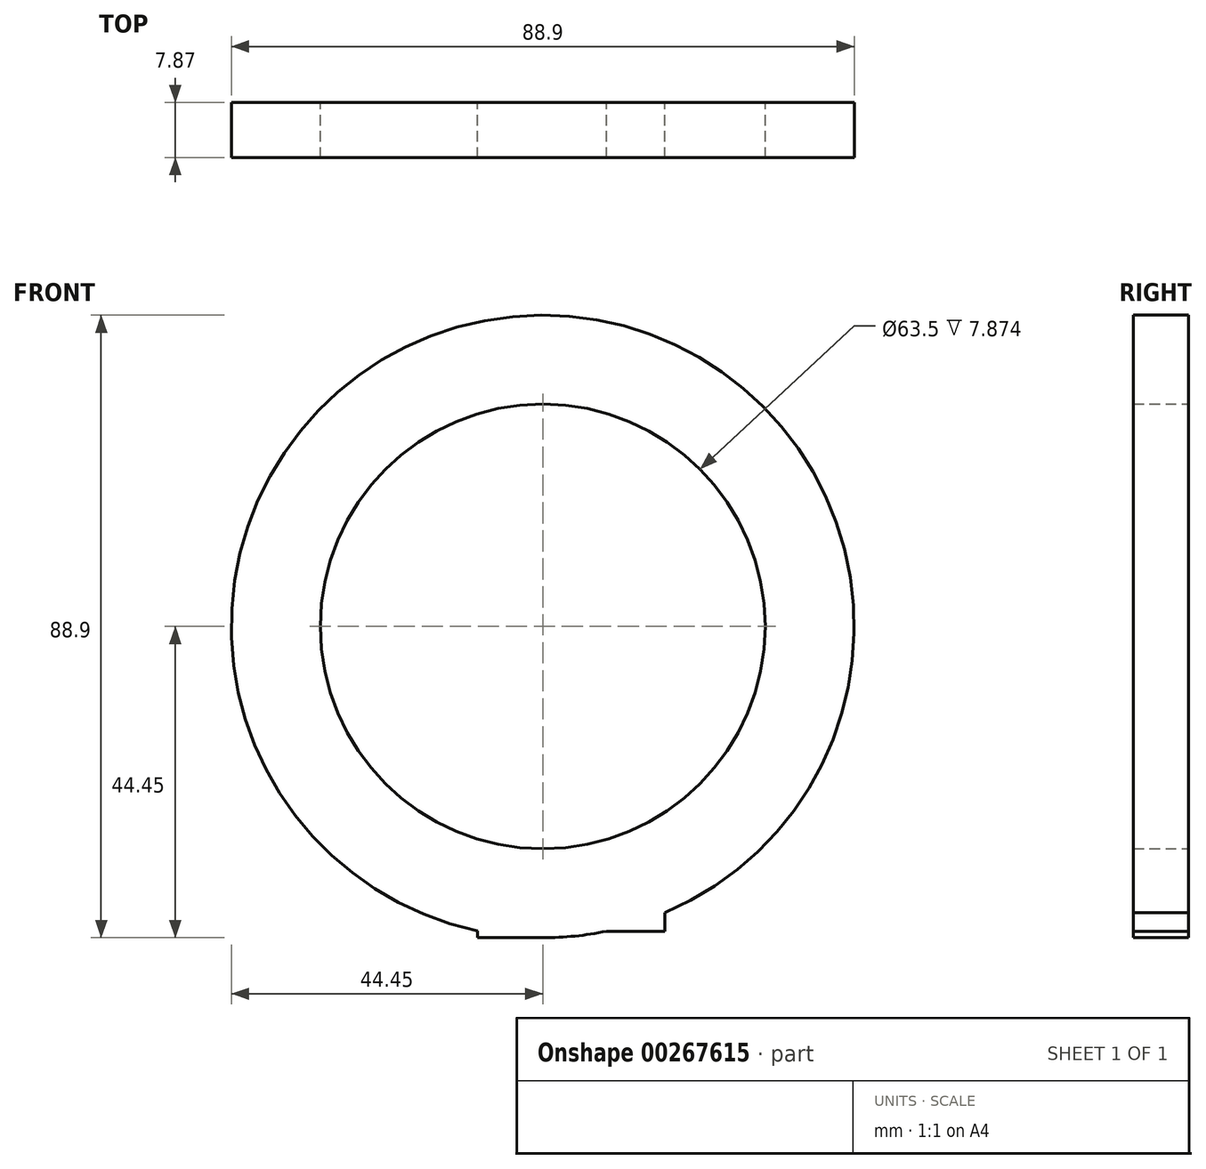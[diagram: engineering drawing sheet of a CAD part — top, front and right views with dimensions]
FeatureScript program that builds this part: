
annotation { "Feature Type Name" : "Feature", "Feature Type Description" : "" }
export const myFeature = defineFeature(function(context is Context, id is Id, definition is map)
    precondition{}
    {
        {
            var Q0;
            Q0=qCreatedBy(makeId("Front.planeOp"),FACE);
            var sketch = newSketch(context, id + "F0", { "sketchPlane" : qUnion([Q0])});
            skCircle(sketch, "E0", {"center": v(0, 0) * mm, "radius": 44.45 * mm});
            skCircle(sketch, "E1", {"center": v(0, 0) * mm, "radius": 31.75 * mm});
            skLineSegment(sketch, "E2.bottom", {"start": v(-9.28, -30.36) * mm, "end": v(0, -30.36) * mm});
            skLineSegment(sketch, "E2.top", {"start": v(-9.28, -44.45) * mm, "end": v(0, -44.45) * mm});
            skLineSegment(sketch, "E2.left", {"start": v(-9.28, -30.36) * mm, "end": v(-9.28, -44.45) * mm});
            skLineSegment(sketch, "E2.right", {"start": v(0, -30.36) * mm, "end": v(0, -44.45) * mm});
            skLineSegment(sketch, "E3.bottom", {"start": v(9.1, -43.5) * mm, "end": v(17.44, -43.5) * mm});
            skLineSegment(sketch, "E3.top", {"start": v(9.1, -26.53) * mm, "end": v(17.44, -26.53) * mm});
            skLineSegment(sketch, "E3.left", {"start": v(9.1, -43.5) * mm, "end": v(9.1, -26.53) * mm});
            skLineSegment(sketch, "E3.right", {"start": v(17.44, -43.5) * mm, "end": v(17.44, -26.53) * mm});
            skSolve(sketch);
        }
        {
            var Q0;
            Q0 = qSketchRegion(id + "F0", true);
            extrude(context, id + "F1", {"entities" : qUnion([Q0]), "depth" : 7.87 * mm});
        }
    });
